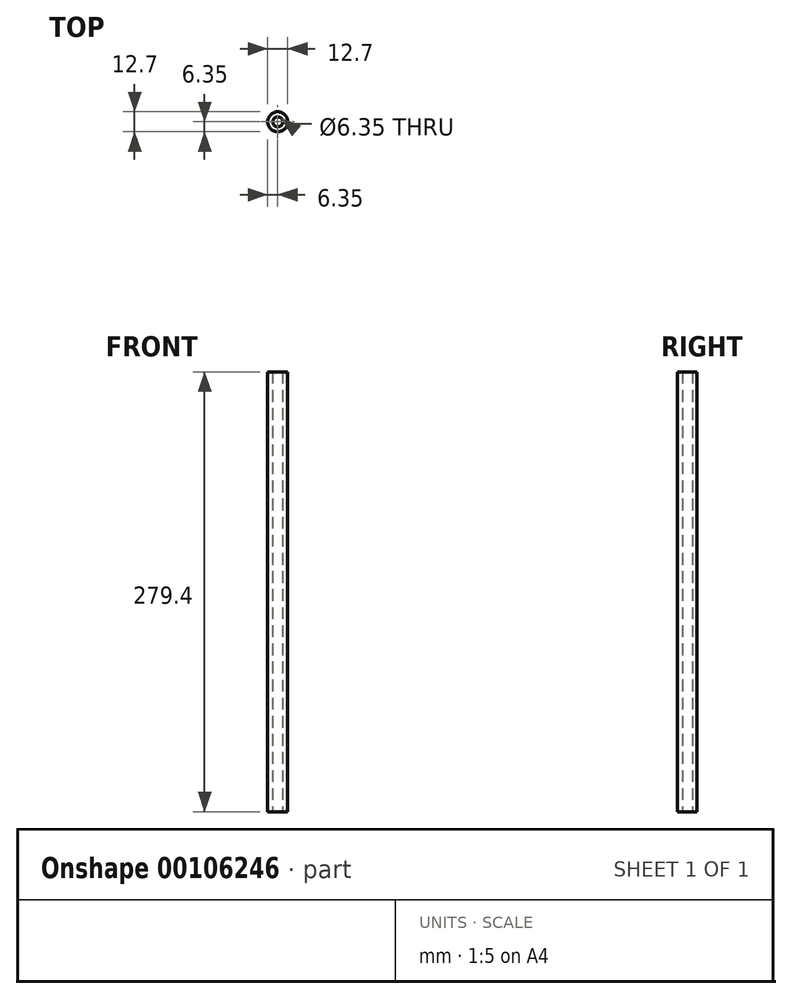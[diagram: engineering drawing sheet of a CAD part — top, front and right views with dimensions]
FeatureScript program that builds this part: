
annotation { "Feature Type Name" : "Feature", "Feature Type Description" : "" }
export const myFeature = defineFeature(function(context is Context, id is Id, definition is map)
    precondition{}
    {
        {
            var Q0;
            Q0=qCreatedBy(makeId("Top.planeOp"),FACE);
            var sketch = newSketch(context, id + "F0", { "sketchPlane" : qUnion([Q0])});
            skCircle(sketch, "E0", {"center": v(0, 0) * mm, "radius": 6.35 * mm});
            skCircle(sketch, "E1", {"center": v(0, 0) * mm, "radius": 3.18 * mm});
            skSolve(sketch);
        }
        {
            var Q0;
            Q0 = qSketchRegion(id + "F0", true);
            extrude(context, id + "F1", {"entities" : qUnion([Q0]), "depth" : 279.4 * mm});
        }
    });
